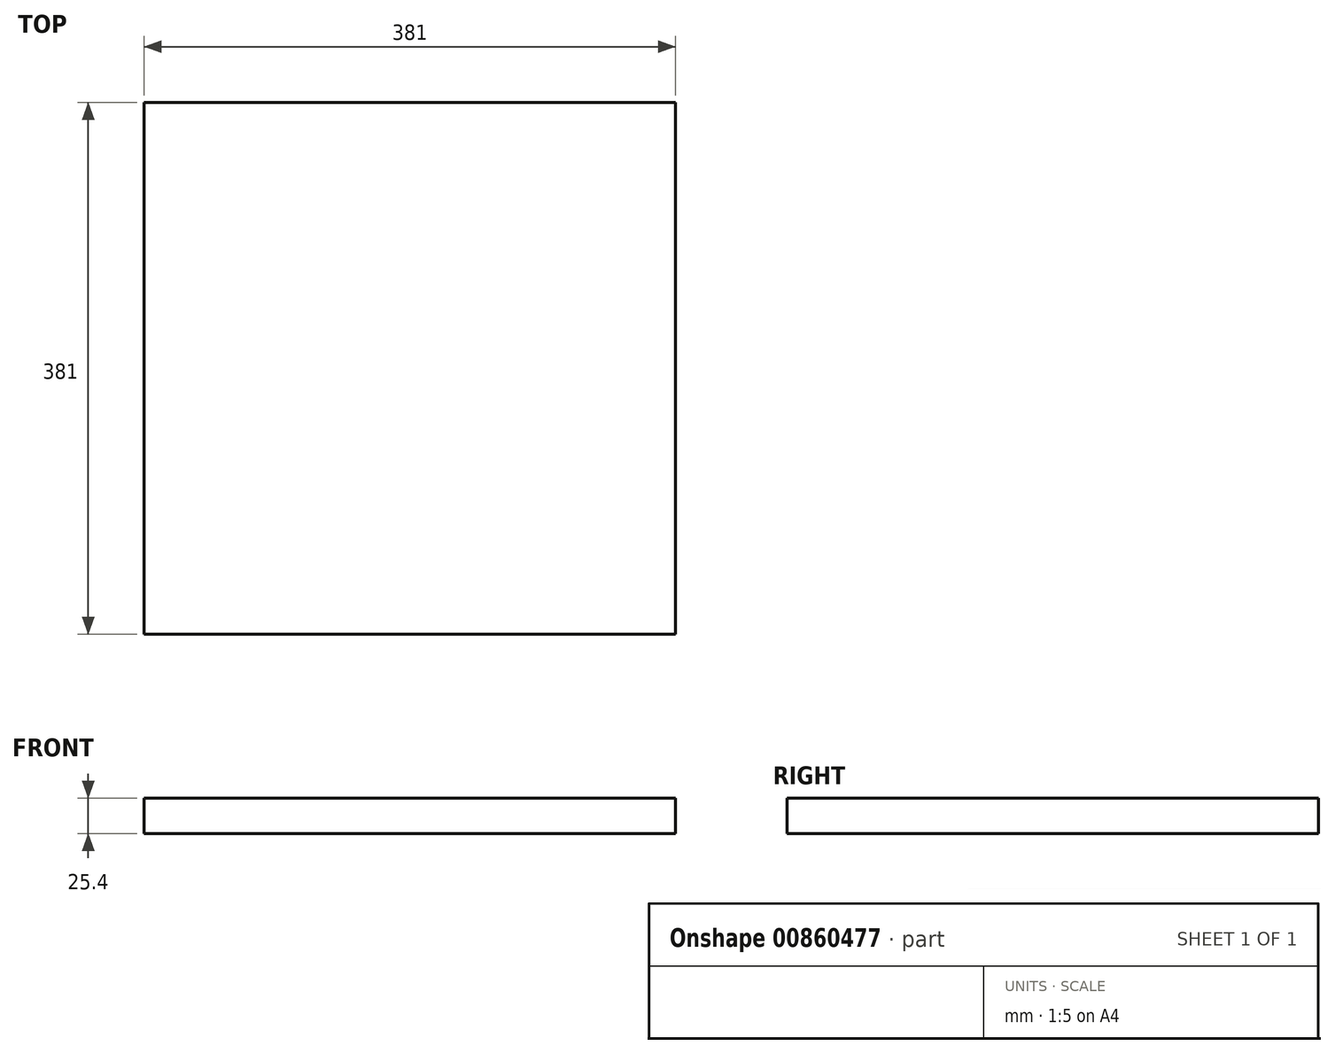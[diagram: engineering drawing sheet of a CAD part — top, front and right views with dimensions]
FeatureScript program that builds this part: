
annotation { "Feature Type Name" : "Feature", "Feature Type Description" : "" }
export const myFeature = defineFeature(function(context is Context, id is Id, definition is map)
    precondition{}
    {
        {
            var Q0;
            Q0=qCreatedBy(makeId("Top.planeOp"),FACE);
            var sketch = newSketch(context, id + "F0", { "sketchPlane" : qUnion([Q0])});
            skLineSegment(sketch, "E0.bottom", {"start": v(190.5, 190.5) * mm, "end": v(-190.5, 190.5) * mm});
            skLineSegment(sketch, "E0.top", {"start": v(190.5, -190.5) * mm, "end": v(-190.5, -190.5) * mm});
            skLineSegment(sketch, "E0.left", {"start": v(190.5, 190.5) * mm, "end": v(190.5, -190.5) * mm});
            skLineSegment(sketch, "E0.right", {"start": v(-190.5, 190.5) * mm, "end": v(-190.5, -190.5) * mm});
            skPoint(sketch, "E0.middle", {"position": v(0, 0) * mm});
            skSolve(sketch);
        }
        {
            var Q0;
            Q0 = qSketchRegion(id + "F0", true);
            extrude(context, id + "F1", {"entities" : qUnion([Q0]), "depth" : 25.4 * mm, "offsetDistance" : 25.4 * mm});
        }
    });
